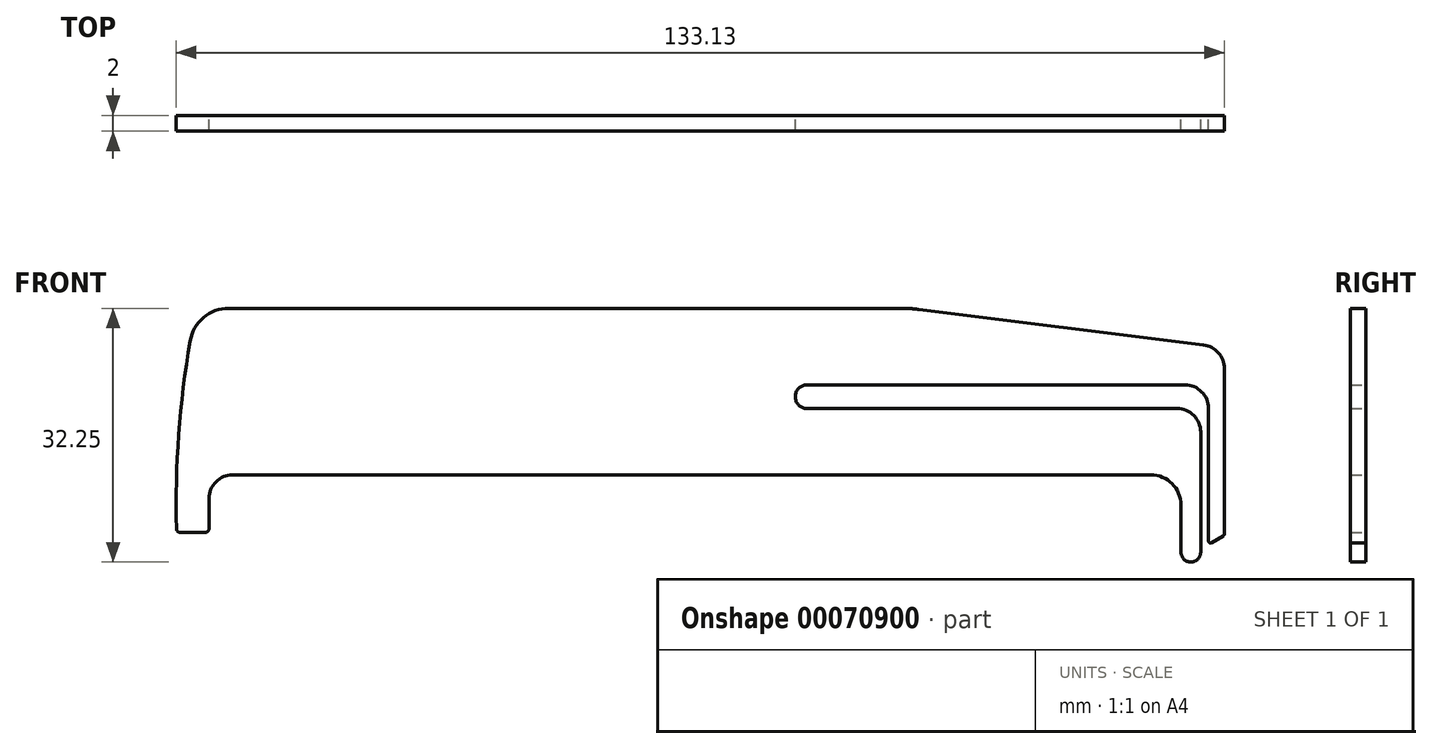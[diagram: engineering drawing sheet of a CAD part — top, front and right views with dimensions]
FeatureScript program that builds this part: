
annotation { "Feature Type Name" : "Feature", "Feature Type Description" : "" }
export const myFeature = defineFeature(function(context is Context, id is Id, definition is map)
    precondition{}
    {
        {
            var Q0;
            Q0=qCreatedBy(makeId("Front.planeOp"),FACE);
            var sketch = newSketch(context, id + "F0", { "sketchPlane" : qUnion([Q0])});
            skCircle(sketch, "E0", {"center": v(-63.82, 0) * mm, "radius": 3.84 * mm});
            skCircle(sketch, "E1", {"center": v(63.82, 0) * mm, "radius": 3.84 * mm, "construction": true});
            skLineSegment(sketch, "E2", {"start": v(-63.82, 0) * mm, "end": v(63.82, 0) * mm, "construction": true});
            skArc(sketch, "E3", {"start": v(-58.22, 20.84) * mm, "mid": v(-59.66, 8.96) * mm, "end": v(-59.95, -3.01) * mm});
            skLineSegment(sketch, "E4", {"start": v(-55.82, -3) * mm, "end": v(-55.82, 0.84) * mm});
            skCircle(sketch, "E5", {"center": v(-51.12, 0) * mm, "radius": 3.84 * mm, "construction": true});
            skCircle(sketch, "E6", {"center": v(76.52, 0) * mm, "radius": 3.84 * mm, "construction": true});
            skLineSegment(sketch, "E7", {"start": v(-73.95, 3.84) * mm, "end": v(-59.92, 3.84) * mm, "construction": true});
            skArc(sketch, "E8", {"start": v(-55.82, 0.84) * mm, "mid": v(-54.94, 2.96) * mm, "end": v(-52.82, 3.84) * mm});
            skLineSegment(sketch, "E9", {"start": v(-53.29, 25) * mm, "end": v(31.9, 25) * mm});
            skLineSegment(sketch, "E10", {"start": v(34.39, 24.85) * mm, "end": v(70.53, 20.33) * mm});
            skLineSegment(sketch, "E11", {"start": v(-52.82, 3.84) * mm, "end": v(63.82, 3.84) * mm});
            skLineSegment(sketch, "E12", {"start": v(67.65, 0) * mm, "end": v(67.65, -6) * mm});
            skLineSegment(sketch, "E13", {"start": v(70.15, -6) * mm, "end": v(70.15, 9.27) * mm});
            skLineSegment(sketch, "E14", {"start": v(67.15, 12.27) * mm, "end": v(20.15, 12.27) * mm});
            skLineSegment(sketch, "E15", {"start": v(20.15, 15.27) * mm, "end": v(68.15, 15.27) * mm});
            skLineSegment(sketch, "E16", {"start": v(71.15, 12.27) * mm, "end": v(71.15, -4.57) * mm});
            skLineSegment(sketch, "E17", {"start": v(71.53, -4.78) * mm, "end": v(73.03, -3.92) * mm});
            skLineSegment(sketch, "E18", {"start": v(73.15, -3.7) * mm, "end": v(73.15, 17.35) * mm});
            skArc(sketch, "E19", {"start": v(20.15, 12.27) * mm, "mid": v(18.65, 13.77) * mm, "end": v(20.15, 15.27) * mm});
            skArc(sketch, "E20", {"start": v(67.65, -6) * mm, "mid": v(68.9, -7.25) * mm, "end": v(70.15, -6) * mm});
            skArc(sketch, "E21", {"start": v(67.65, 0) * mm, "mid": v(66.53, 2.71) * mm, "end": v(63.82, 3.84) * mm});
            skPoint(sketch, "E22.visualSharp", {"position": v(71.15, -5) * mm});
            skArc(sketch, "E22.filletArc", {"start": v(71.15, -4.57) * mm, "mid": v(71.28, -4.78) * mm, "end": v(71.53, -4.78) * mm});
            skPoint(sketch, "E23.visualSharp", {"position": v(73.15, -3.85) * mm});
            skArc(sketch, "E23.filletArc", {"start": v(73.03, -3.92) * mm, "mid": v(73.12, -3.83) * mm, "end": v(73.15, -3.7) * mm});
            skPoint(sketch, "E24.visualSharp", {"position": v(70.15, 12.27) * mm});
            skArc(sketch, "E24.filletArc", {"start": v(70.15, 9.27) * mm, "mid": v(69.27, 11.4) * mm, "end": v(67.15, 12.27) * mm});
            skPoint(sketch, "E25.visualSharp", {"position": v(71.15, 15.27) * mm});
            skArc(sketch, "E25.filletArc", {"start": v(71.15, 12.27) * mm, "mid": v(70.27, 14.4) * mm, "end": v(68.15, 15.27) * mm});
            skPoint(sketch, "E26.visualSharp", {"position": v(73.15, 20) * mm});
            skArc(sketch, "E26.filletArc", {"start": v(73.15, 17.35) * mm, "mid": v(72.4, 19.34) * mm, "end": v(70.53, 20.33) * mm});
            skPoint(sketch, "E27.visualSharp", {"position": v(33.15, 25) * mm});
            skArc(sketch, "E27.filletArc", {"start": v(34.39, 24.85) * mm, "mid": v(33.15, 24.96) * mm, "end": v(31.9, 25) * mm});
            skPoint(sketch, "E28.visualSharp", {"position": v(-57.43, 25) * mm});
            skArc(sketch, "E28.filletArc", {"start": v(-53.29, 25) * mm, "mid": v(-56.51, 23.82) * mm, "end": v(-58.22, 20.84) * mm});
            skLineSegment(sketch, "E29", {"start": v(-59.45, -3.5) * mm, "end": v(-56.32, -3.5) * mm});
            skPoint(sketch, "E30.visualSharp", {"position": v(-59.93, -3.5) * mm});
            skArc(sketch, "E30.filletArc", {"start": v(-59.95, -3.01) * mm, "mid": v(-59.8, -3.36) * mm, "end": v(-59.45, -3.5) * mm});
            skPoint(sketch, "E31.visualSharp", {"position": v(-55.82, -3.5) * mm});
            skArc(sketch, "E31.filletArc", {"start": v(-56.32, -3.5) * mm, "mid": v(-55.96, -3.35) * mm, "end": v(-55.82, -3) * mm});
            skCircle(sketch, "E32", {"center": v(76.58, 0) * mm, "radius": 3.84 * mm, "construction": true});
            skSolve(sketch);
        }
        {
            var Q0;
            {var subQ0=sQuery(id+"F0.wireOp",EDGE,"E4");Q0=makeQuery(id+"F0.imprint","IMPRINT",FACE,{"disambiguationData":[TD([[makeQuery(id+"F0.imprint","IMPRINT",EDGE,{"derivedFrom":subQ0}),1.0]])]});}
            var Q1;
            {var subQ0=sQuery(id+"F0.wireOp",EDGE,"7947a128-3fcc-45af-b4ab-035d31c2ea50");var subQ1=sQuery(id+"F0.wireOp",EDGE,"E3");var subQ2=makeQuery(id+"F0.imprint","INTERSECT",VERTEX,{"disambiguationData":[OD(0.0)],"derivedFrom":[subQ1,subQ0]});Q1=makeQuery(id+"F0.imprint","IMPRINT",FACE,{"disambiguationData":[TD([[makeQuery(id+"F0.imprint","IMPRINT",EDGE,{"disambiguationData":[TD([[subQ2,1.0]])],"derivedFrom":subQ1}),-1.0]])]});}
            extrude(context, id + "F1", {"entities" : qUnion([Q0, Q1]), "endBound" : BoundingType.SYMMETRIC, "depth" : 2 * mm});
        }
    });
